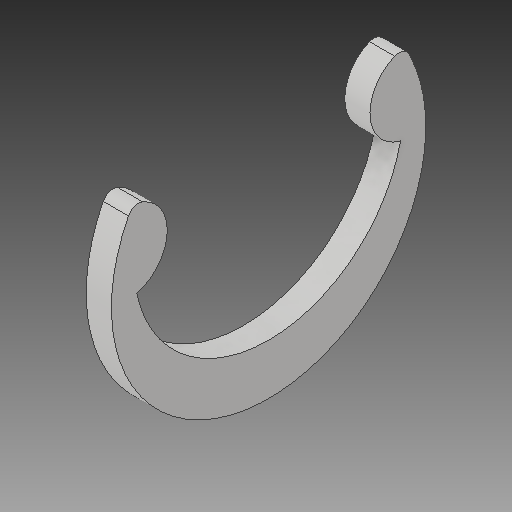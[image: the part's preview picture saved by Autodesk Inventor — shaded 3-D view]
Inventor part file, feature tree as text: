
AUTODESK INVENTOR PART (.ipt)
format: ipt  version: 2017 (Build 210142000, 142)  size: 89,600 bytes
history: native  units: in
note: dims shown in document units (in); Inventor stores cm internally (conversion verified against a paired STEP export)
features: extrude x1
ambient origin geometry x8: Origin, YZ Plane, XZ Plane, XY Plane, X Axis, Y Axis, Z Axis, Center Point
bodies: Solid1 (feature_tree)
feature tree (1):
  extrude  "Extrude1"  [1 undecoded]
note: 1 required parameter value undecoded (feature->parameter linkage not recoverable at this tier; creation-order binding heuristic only, values carry confidence <= 0.55)
